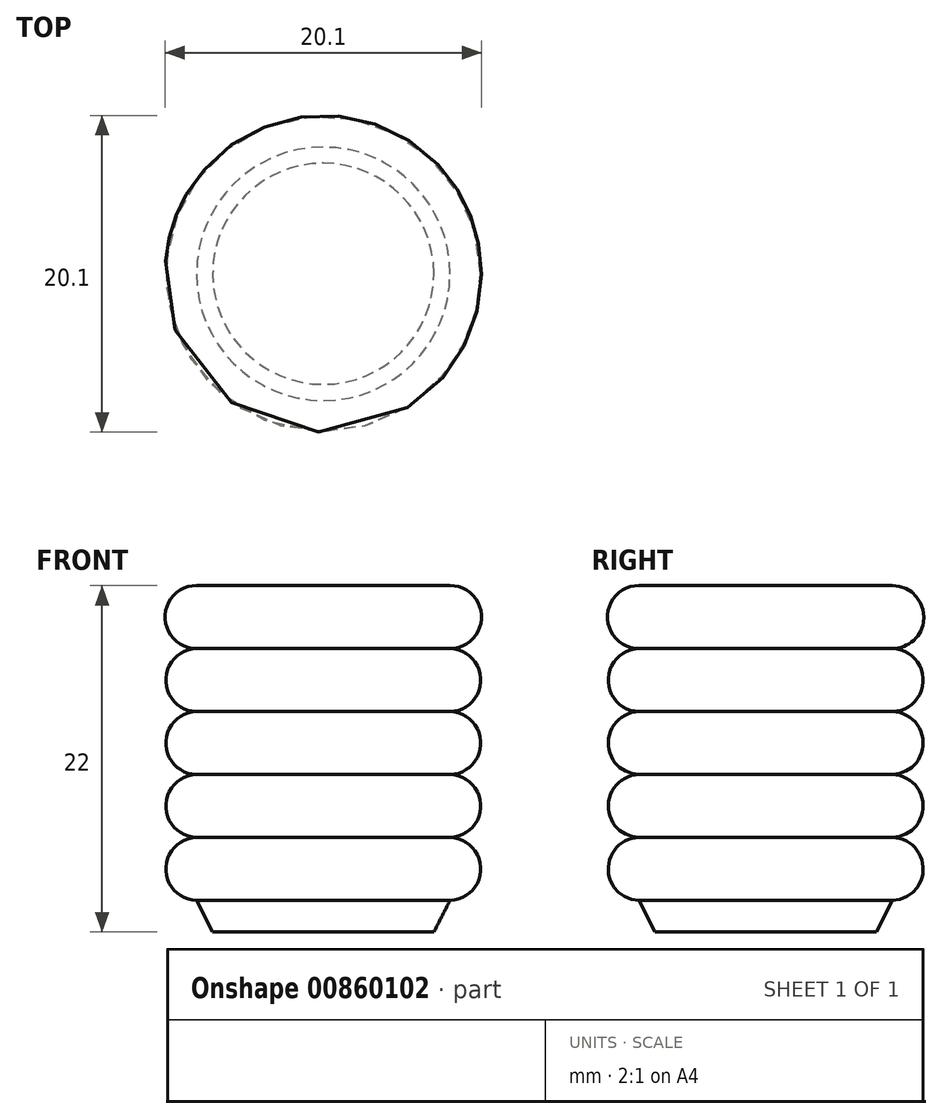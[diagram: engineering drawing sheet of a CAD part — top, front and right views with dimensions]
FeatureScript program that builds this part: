
annotation { "Feature Type Name" : "Feature", "Feature Type Description" : "" }
export const myFeature = defineFeature(function(context is Context, id is Id, definition is map)
    precondition{}
    {
        {
            var Q0;
            Q0=qCreatedBy(makeId("Front.planeOp"),FACE);
            var sketch = newSketch(context, id + "F0", { "sketchPlane" : qUnion([Q0])});
            skLineSegment(sketch, "E0", {"start": v(0, 41.07) * mm, "end": v(0, -40.87) * mm, "construction": true});
            skLineSegment(sketch, "E1", {"start": v(-41.07, 0) * mm, "end": v(0, 0) * mm, "construction": true});
            skLineSegment(sketch, "E2.bottom", {"start": v(7.95, 0) * mm, "end": v(10, 0) * mm});
            skLineSegment(sketch, "E2.top", {"start": v(0, 20) * mm, "end": v(8.05, 20) * mm});
            skLineSegment(sketch, "E2.left", {"start": v(0, 0) * mm, "end": v(0, 20) * mm});
            skArc(sketch, "E3", {"start": v(8, 16) * mm, "mid": v(10.05, 17.97) * mm, "end": v(8.05, 20) * mm});
            skPoint(sketch, "E3.first.point", {"position": v(8.05, 20) * mm});
            skPoint(sketch, "E3.second.point", {"position": v(10, 18.45) * mm});
            skPoint(sketch, "E3.third.point", {"position": v(8.05, 16) * mm});
            skPoint(sketch, "E4", {"position": v(10, 14) * mm});
            skArc(sketch, "E5", {"start": v(7.95, 12) * mm, "mid": v(10, 13.97) * mm, "end": v(8, 16) * mm});
            skPoint(sketch, "E5.third.point", {"position": v(8.05, 12) * mm});
            skPoint(sketch, "E6", {"position": v(10, 10) * mm});
            skPoint(sketch, "E7", {"position": v(10, 6) * mm});
            skPoint(sketch, "E8", {"position": v(10, 2) * mm});
            skArc(sketch, "E9", {"start": v(7.95, 8) * mm, "mid": v(10, 10) * mm, "end": v(7.95, 12) * mm});
            skPoint(sketch, "E9.third.point", {"position": v(8.05, 8) * mm});
            skArc(sketch, "E10", {"start": v(7.95, 4) * mm, "mid": v(10, 6) * mm, "end": v(7.95, 8) * mm});
            skPoint(sketch, "E10.third.point", {"position": v(8.05, 4) * mm});
            skArc(sketch, "E11", {"start": v(7.95, 0) * mm, "mid": v(10, 2) * mm, "end": v(7.95, 4) * mm});
            skPoint(sketch, "E11.third.point", {"position": v(8.05, 0) * mm});
            skLineSegment(sketch, "E12", {"start": v(0, -2) * mm, "end": v(7.02, -2) * mm});
            skLineSegment(sketch, "E13", {"start": v(7.02, -2) * mm, "end": v(8.05, 0) * mm});
            skLineSegment(sketch, "E14", {"start": v(0, 0) * mm, "end": v(0, -2) * mm});
            skLineSegment(sketch, "E15.trimOffspring", {"start": v(7.95, 0) * mm, "end": v(41.07, 0) * mm, "construction": true});
            skSolve(sketch);
        }
        {
            var Q0;
            Q0 = qSketchRegion(id + "F0", true);
            var Q1;
            Q1=sQuery(id+"F0.wireOp",EDGE,"E0");
            revolve(context, id + "F1", {"surfaceOperationType" : NewSurfaceOperationType.NEW, "entities" : qUnion([Q0]), "axis" : qUnion([Q1]), "revolveType" : RevolveType.FULL});
        }
    });
